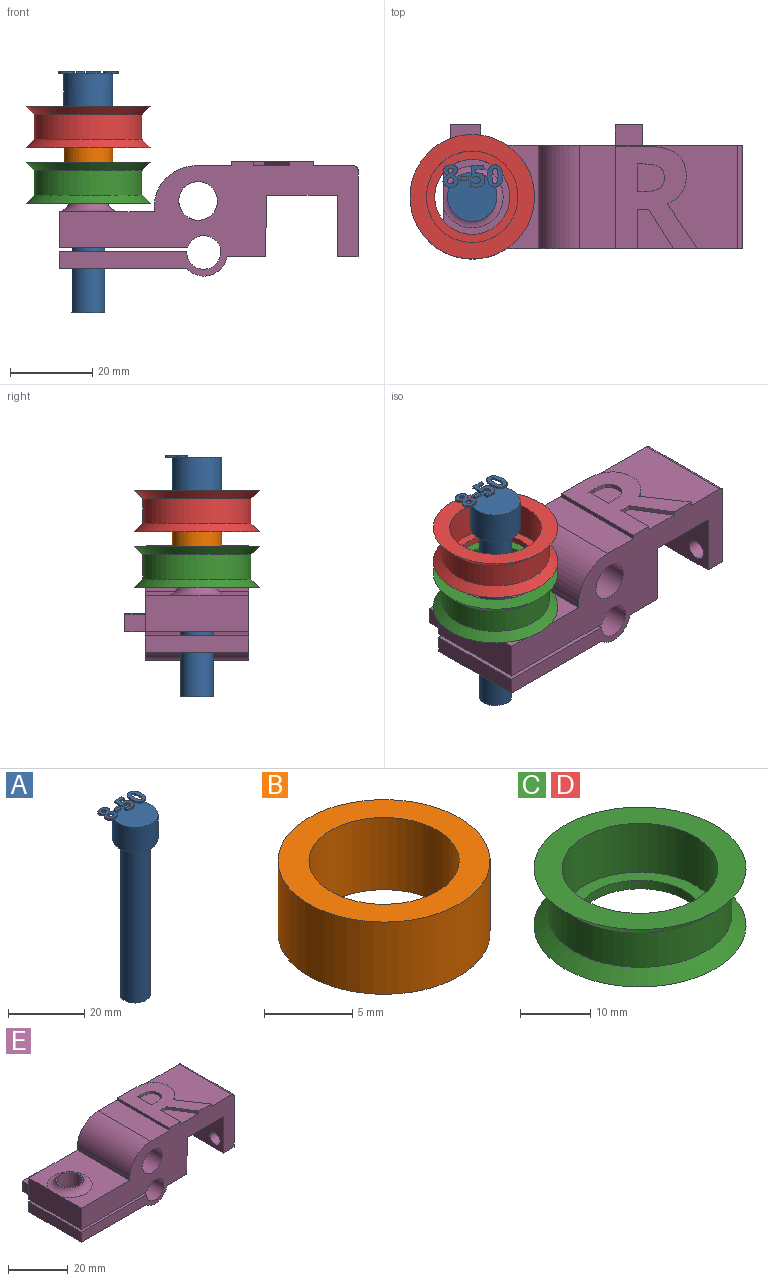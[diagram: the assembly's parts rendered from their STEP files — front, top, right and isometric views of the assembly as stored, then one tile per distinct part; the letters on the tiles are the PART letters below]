
ASSEMBLY  parts=5 mates=4
PART A: 86 faces, bbox 14.5x13.7x58.5 mm
  f0: plane 12x12mm, normal (0,0,1), area 99.4mm2, adj f5,f22,f23,f24,f25,f26,f40,f41
  f1: plane 1x0.26mm, normal (0,0,1), area 0.1mm2, adj f5,f46,f47,f48,f49
  f2: plane 0.85x0.68mm, normal (0,0,1), area 0.2mm2, adj f5,f29,f30,f31
  f3: cylinder r=4mm len=50mm, axis (0,0,-1), area 1256.6mm2, adj f4,f6
  f4: plane 8x8mm, normal (0,0,-1), area 50.3mm2, adj f3
  f5: cylinder r=6mm len=12mm, axis (0,0,-1), area 301.6mm2, adj f0,f1,f2,f6,f39,f45,f67,f85
  f6: plane 12x12mm, normal (0,0,-1), area 62.8mm2, adj f3,f5
  f7: extruded ~0.5x0.46mm, area 0.2mm2, adj f8,f37,f38,f39
  f8: extruded ~0.5x0.46mm, area 0.2mm2, adj f7,f9,f38,f39
  f9: extruded ~0.5x0.39mm, area 0.2mm2, adj f8,f10,f38,f39
  f10: extruded ~0.5x0.4mm, area 0.2mm2, adj f9,f11,f38,f39
  f11: extruded ~0.5x0.49mm, area 0.3mm2, adj f10,f12,f38,f39
  f12: extruded ~0.5x0.5mm, area 0.3mm2, adj f11,f13,f38,f39
  f13: extruded ~0.5x0.39mm, area 0.2mm2, adj f12,f37,f38,f39
  f14: extruded ~1.22x0.5mm, area 0.6mm2, adj f15,f35,f38,f39
  f15: extruded ~1.22x0.5mm, area 0.6mm2, adj f14,f16,f38,f39
  f16: extruded ~0.91x0.5mm, area 0.5mm2, adj f15,f17,f38,f39
  f17: extruded ~0.71x0.5mm, area 0.4mm2, adj f16,f18,f38,f39
  f18: extruded ~0.65x0.61mm, area 0.4mm2, adj f17,f19,f38,f39
  f19: extruded ~0.77x0.62mm, area 0.5mm2, adj f18,f20,f38,f39
  f20: extruded ~0.8x0.5mm, area 0.4mm2, adj f19,f21,f38,f39
  f21: extruded ~1.04x0.5mm, area 0.6mm2, adj f20,f22,f38,f39
  f22: extruded ~1.36x0.5mm, area 0.7mm2, adj f0,f21,f23,f38,f39
  f23: extruded ~1.33x0.5mm, area 0.7mm2, adj f0,f22,f24,f38
  f24: extruded ~1.04x0.51mm, area 0.6mm2, adj f0,f23,f25,f38
  f25: extruded ~0.75x0.5mm, area 0.4mm2, adj f0,f24,f26,f38
  f26: extruded ~0.85x0.66mm, area 0.5mm2, adj f0,f25,f27,f38,f39
  f27: extruded ~0.72x0.56mm, area 0.5mm2, adj f26,f28,f38,f39
  f28: extruded ~0.72x0.5mm, area 0.4mm2, adj f27,f35,f38,f39
  f29: extruded ~0.5x0.45mm, area 0.3mm2, adj f2,f30,f36,f38,f39
  f30: extruded ~0.5x0.47mm, area 0.3mm2, adj f2,f29,f31,f38
  f31: extruded ~0.62x0.5mm, area 0.3mm2, adj f2,f30,f32,f38,f39
  f32: extruded ~0.59x0.5mm, area 0.3mm2, adj f31,f33,f38,f39
  f33: extruded ~0.5x0.48mm, area 0.3mm2, adj f32,f34,f38,f39
  f34: extruded ~0.89x0.77mm, area 0.6mm2, adj f33,f36,f38,f39
  f35: extruded ~0.93x0.5mm, area 0.5mm2, adj f14,f28,f38,f39
  f36: extruded ~0.66x0.5mm, area 0.4mm2, adj f29,f34,f38,f39
  f37: extruded ~0.5x0.39mm, area 0.2mm2, adj f7,f13,f38,f39
  f38: plane 5.4x3.69mm, normal (0,0,1), area 12.7mm2, adj f7,f8,f9,f10,f11,f12,f13,f14
  f39: plane 5.4x3.53mm, normal (0,0,-1), area 10.2mm2, adj f5,f7,f8,f9,f10,f11,f12,f13
  f40: plane 0.9x0.5mm, normal (-1,0,0), area 0.4mm2, adj f0,f41,f43,f44
  f41: plane 1.93x0.5mm, normal (0,-1,0), area 1mm2, adj f0,f40,f42,f44
  f42: plane 0.9x0.5mm, normal (1,0,0), area 0.4mm2, adj f0,f41,f43,f44
  f43: plane 1.93x0.5mm, normal (0,1,0), area 1mm2, adj f0,f40,f42,f44
  f44: plane 1.93x0.9mm, normal (0,0,1), area 1.7mm2, adj f40,f41,f42,f43
  f45: plane 0.76x0.31mm, normal (0,0,-1), area 0mm2, adj f5,f46
  f46: extruded ~1.21x0.5mm, area 0.7mm2, adj f0,f1,f45,f47,f65,f66
  f47: extruded ~0.54x0.5mm, area 0.3mm2, adj f1,f46,f48,f66
  f48: plane 0.5x0.13mm, normal (-0.2,0.98,0), area 0.1mm2, adj f1,f47,f49,f66
  f49: plane 1.03x0.5mm, normal (1,-0.09,0), area 0.5mm2, adj f1,f48,f50,f66,f67
  f50: plane 1.88x0.5mm, normal (0,-1,0), area 0.9mm2, adj f49,f51,f66,f67
  f51: plane 0.94x0.5mm, normal (1,0,0), area 0.5mm2, adj f50,f52,f66,f67
  f52: plane 2.85x0.5mm, normal (0,1,0), area 1.4mm2, adj f51,f53,f66,f67
  f53: plane 2.68x0.5mm, normal (-1,0.07,0), area 1.3mm2, adj f0,f52,f54,f66,f67
  f54: plane 0.5x0.44mm, normal (-0.47,-0.88,0), area 0.3mm2, adj f0,f53,f55,f66
  f55: extruded ~0.5x0.37mm, area 0.2mm2, adj f0,f54,f56,f66
  f56: extruded ~0.5x0.42mm, area 0.2mm2, adj f0,f55,f57,f66
  f57: extruded ~1.05x0.8mm, area 0.8mm2, adj f0,f56,f58,f66
  f58: extruded ~1.02x0.83mm, area 0.8mm2, adj f0,f57,f59,f66
  f59: extruded ~0.72x0.5mm, area 0.4mm2, adj f0,f58,f60,f66
  f60: extruded ~0.66x0.5mm, area 0.4mm2, adj f0,f59,f61,f66
  f61: plane 0.96x0.5mm, normal (-1,0,0), area 0.5mm2, adj f0,f60,f62,f66
  f62: extruded ~1.42x0.5mm, area 0.7mm2, adj f0,f61,f63,f66
  f63: extruded ~1.55x0.5mm, area 0.8mm2, adj f0,f62,f64,f66
  f64: extruded ~1.36x0.54mm, area 0.8mm2, adj f0,f63,f65,f66
  f65: extruded ~1.17x0.5mm, area 0.6mm2, adj f0,f46,f64,f66
  f66: plane 5.33x3.51mm, normal (0,0,1), area 10.9mm2, adj f46,f47,f48,f49,f50,f51,f52,f53
  f67: plane 2.97x1.71mm, normal (0,0,-1), area 3.5mm2, adj f5,f49,f50,f51,f52,f53
  f68: extruded ~1.39x0.5mm, area 0.7mm2, adj f69,f83,f84,f85
  f69: extruded ~1.39x0.5mm, area 0.7mm2, adj f68,f70,f84,f85
  f70: extruded ~0.56x0.5mm, area 0.4mm2, adj f69,f71,f84,f85
  f71: extruded ~0.56x0.5mm, area 0.4mm2, adj f70,f72,f84,f85
  f72: extruded ~1.39x0.5mm, area 0.7mm2, adj f71,f73,f84,f85
  f73: extruded ~1.38x0.5mm, area 0.7mm2, adj f72,f74,f84,f85
  f74: extruded ~0.56x0.5mm, area 0.4mm2, adj f73,f83,f84,f85
  f75: extruded ~2.04x0.5mm, area 1.1mm2, adj f76,f82,f84,f85
  f76: extruded ~2.02x0.5mm, area 1.1mm2, adj f75,f77,f84,f85
  f77: extruded ~1.38x0.69mm, area 0.8mm2, adj f76,f78,f84,f85
  f78: extruded ~1.38x0.66mm, area 0.8mm2, adj f77,f79,f84,f85
  f79: extruded ~2.05x0.5mm, area 1.1mm2, adj f78,f80,f84,f85
  f80: extruded ~2.02x0.5mm, area 1mm2, adj f0,f79,f81,f84,f85
  f81: extruded ~1.37x0.68mm, area 0.8mm2, adj f0,f80,f82,f84
  f82: extruded ~1.39x0.66mm, area 0.8mm2, adj f0,f75,f81,f84,f85
  f83: extruded ~0.56x0.5mm, area 0.4mm2, adj f68,f74,f84,f85
  f84: plane 5.41x3.68mm, normal (0,0,1), area 12.1mm2, adj f68,f69,f70,f71,f72,f73,f74,f75
  f85: plane 5.41x3.68mm, normal (0,0,-1), area 10.3mm2, adj f5,f68,f69,f70,f71,f72,f73,f74
PART B: 4 faces, bbox 12x12x5 mm
  f0: cylinder r=4.25mm len=8.5mm, axis (0,0,-1), area 133.5mm2, adj f2,f3
  f1: cylinder r=6mm len=12mm, axis (0,0,-1), area 188.5mm2, adj f2,f3
  f2: plane 12x12mm, normal (0,0,1), area 56.4mm2, adj f0,f1
  f3: plane 12x12mm, normal (0,0,-1), area 56.4mm2, adj f0,f1
PART C: 8 faces, bbox 30.2x30.2x10 mm
  f0: plane 30.2x30.2mm, normal (0,0,1), area 329.2mm2, adj f1,f7
  f1: cylinder r=11.1mm len=22.2mm, axis (0,0,-1), area 592.8mm2, adj f0,f2
  f2: plane 22.2x22.2mm, normal (0,0,1), area 126.9mm2, adj f1,f3
  f3: cylinder r=9.1mm len=18.2mm, axis (0,0,-1), area 85.8mm2, adj f2,f4
  f4: plane 30.2x30.2mm, normal (0,0,-1), area 456.2mm2, adj f3,f5
  f5: cone r=13.1mm half-angle=45deg, axis (0,0,-1), area 250.6mm2, adj f4,f6
  f6: cylinder r=13.1mm len=26.2mm, axis (0,0,-1), area 493.9mm2, adj f5,f7
  f7: cone r=15.1mm half-angle=45deg, axis (0,0,1), area 250.6mm2, adj f0,f6
PART D: same geometry as C
PART E: 56 faces, bbox 75.9x30x27.7 mm
  f0: plane 38.42x25mm, normal (0,0,1), area 567.1mm2, adj f14,f15,f25,f27,f40,f41,f42,f43
  f1: plane 9.51x8.71mm, normal (0,0,1), area 54.7mm2, adj f14,f37,f38,f39
  f2: plane 25x4.12mm, normal (-1,0,0), area 103mm2, adj f5,f14,f15,f19
  f3: cylinder r=4.17mm len=8.35mm, axis (0,0,1), area 108.1mm2, adj f5,f19
  f4: plane 25x9.34mm, normal (0,0,-1), area 233.4mm2, adj f13,f14,f15,f17
  f5: plane 30.88x25mm, normal (0,0,-1), area 717.2mm2, adj f2,f3,f14,f15,f17
  f6: plane 25x8.82mm, normal (-1,0,0), area 219.6mm2, adj f7,f14,f15,f20,f24
  f7: plane 25x23mm, normal (0,0,1), area 400mm2, adj f6,f8,f14,f15,f24
  f8: plane 25x1.1mm, normal (-1,0,0), area 27.5mm2, adj f7,f14,f15,f25
  f9: plane 25x21.09mm, normal (1,0,0), area 493.5mm2, adj f10,f14,f15,f22,f23,f27
  f10: plane 25x5mm, normal (0,0,-1), area 125mm2, adj f9,f11,f14,f15
  f11: plane 25x15mm, normal (-1,0,0), area 341.3mm2, adj f10,f12,f14,f15,f22,f23
  f12: plane 25x17.2mm, normal (0,0,-1), area 430mm2, adj f11,f13,f14,f15
  f13: plane 25x14.91mm, normal (1,0,-0.01), area 372.8mm2, adj f4,f12,f14,f15
  f14: plane 72.42x27.75mm, normal (0,-1,0), area 1047.5mm2, adj f0,f1,f2,f4,f5,f6,f7,f8
  f15: plane 72.42x26.75mm, normal (0,1,0), area 976.4mm2, adj f0,f2,f4,f5,f6,f7,f8,f9
  f16: cylinder r=4.17mm len=10.78mm, axis (0,0,1), area 282.8mm2, adj f20,f21
  f17: cylinder r=5.75mm len=25mm, axis (0,-1,0), area 315.9mm2, adj f4,f5,f14,f15
  f18: cylinder r=4.1mm len=25mm, axis (0,-1,0), area 618.7mm2, adj f14,f15,f19,f20
  f19: plane 30.91x25mm, normal (0,0,1), area 718.1mm2, adj f2,f3,f14,f15,f18
  f20: plane 31.07x30mm, normal (0,0,-1), area 758.4mm2, adj f6,f14,f15,f16,f18,f29,f30,f31
  f21: plane 9.35x9.35mm, normal (0,0,1), area 13.9mm2, adj f16,f24
  f22: cylinder r=2.43mm len=5mm, axis (1,0,0), area 76.2mm2, adj f9,f11
  f23: cylinder r=2.2mm len=5mm, axis (1,0,0), area 69.1mm2, adj f9,f11
  f24: torus R=7.5mm, axis (0,0,-1), area 134.6mm2, adj f6,f7,f21
  f25: cylinder r=10mm len=25mm, axis (0,-1,0), area 392.7mm2, adj f0,f8,f14,f15
  f26: cylinder r=4.68mm len=25mm, axis (0,-1,0), area 735.2mm2, adj f14,f15
  f27: cylinder r=1mm len=25mm, axis (0,-1,0), area 39.3mm2, adj f0,f9,f14,f15
  f28: plane 7.3x5mm, normal (0,0,1), area 36.5mm2, adj f15,f29,f30,f31
  f29: plane 5x4.12mm, normal (-1,0,0), area 20.6mm2, adj f15,f20,f28,f31
  f30: plane 5x4.12mm, normal (1,0,0), area 20.6mm2, adj f15,f20,f28,f31
  f31: plane 7.3x4.12mm, normal (0,1,0), area 30.1mm2, adj f20,f28,f29,f30
  f32: plane 6.63x5mm, normal (0,0,1), area 33.2mm2, adj f15,f33,f35,f36
  f33: plane 5x4.5mm, normal (-1,0,0), area 22.5mm2, adj f15,f32,f34,f36
  f34: plane 6.63x5mm, normal (0,0,-1), area 33.2mm2, adj f15,f33,f35,f36
  f35: plane 5x4.5mm, normal (1,0,0), area 22.5mm2, adj f15,f32,f34,f36
  f36: plane 6.63x4.5mm, normal (0,1,0), area 29.9mm2, adj f32,f33,f34,f35
  f37: plane 9.51x1mm, normal (1,0,0), area 9.5mm2, adj f1,f14,f38,f54
  f38: plane 2.79x1mm, normal (0,-1,0), area 2.8mm2, adj f1,f37,f39,f54
  f39: plane 9.51x5.92mm, normal (-0.85,-0.53,0), area 11.2mm2, adj f1,f14,f38,f54
  f40: extruded ~10.8x7.29mm, area 13mm2, adj f0,f14,f41,f54
  f41: extruded ~3.41x2.67mm, area 4.4mm2, adj f0,f40,f42,f54
  f42: extruded ~3.89x1.2mm, area 4.1mm2, adj f0,f41,f43,f54
  f43: extruded ~5.59x2.42mm, area 6.3mm2, adj f0,f42,f44,f54
  f44: extruded ~7.48x1.84mm, area 7.8mm2, adj f0,f43,f45,f54
  f45: plane 7.22x1mm, normal (0,1,0), area 7.2mm2, adj f0,f44,f46,f54
  f46: plane 24.79x1mm, normal (-1,0,0), area 24.8mm2, adj f0,f14,f45,f54
  f47: plane 1.69x1mm, normal (0,1,0), area 1.7mm2, adj f48,f53,f54,f55
  f48: plane 6.7x1mm, normal (1,0,0), area 6.7mm2, adj f47,f49,f54,f55
  f49: plane 1.6x1mm, normal (0,-1,0), area 1.6mm2, adj f48,f50,f54,f55
  f50: extruded ~3.75x1mm, area 3.9mm2, adj f49,f51,f54,f55
  f51: extruded ~2.51x1.21mm, area 2.9mm2, adj f50,f52,f54,f55
  f52: extruded ~2.61x1.19mm, area 3mm2, adj f51,f53,f54,f55
  f53: extruded ~3.68x1mm, area 3.8mm2, adj f47,f52,f54,f55
  f54: plane 24.79x19.8mm, normal (0,0,1), area 300mm2, adj f14,f37,f38,f39,f40,f41,f42,f43
  f55: plane 6.7x6.56mm, normal (0,0,1), area 38.8mm2, adj f47,f48,f49,f50,f51,f52,f53
PLACE A t=(-103.78,-12.5,-13.6)mm
PLACE B rot(axis=(1,0,0),180deg) t=(-103.78,-12.5,26.4)mm
PLACE C t=(-103.78,-12.5,18.1)mm
PLACE D t=(-103.78,-12.5,31.6)mm
PLACE E at identity
MATE fastened A.f3 <-> D.f1  axis (0,0,-1) through (-103.78,-12.5,36.4)mm
MATE fastened B.f0 <-> C.f1  axis (0,0,1) through (-103.78,-12.5,21.4)mm
MATE fastened C.f1 <-> E.f3  axis (0,0,-1) through (-103.78,-12.5,12.9)mm
MATE fastened D.f1 <-> B.f0  axis (0,0,-1) through (-103.78,-12.5,26.4)mm
